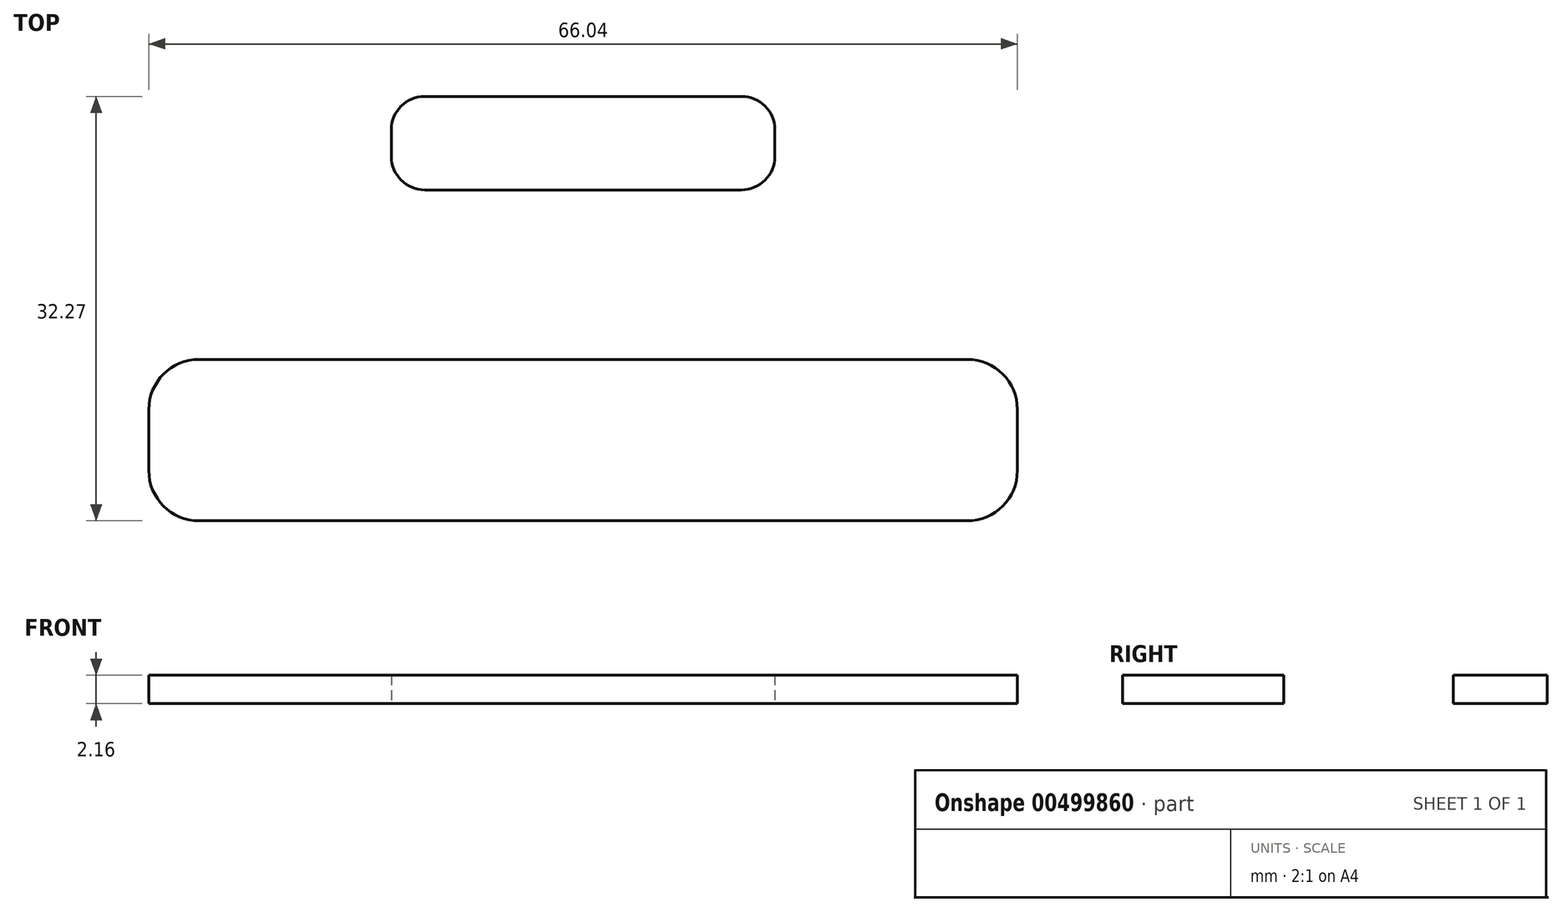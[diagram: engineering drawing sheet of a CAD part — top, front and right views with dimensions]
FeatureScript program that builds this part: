
annotation { "Feature Type Name" : "Feature", "Feature Type Description" : "" }
export const myFeature = defineFeature(function(context is Context, id is Id, definition is map)
    precondition{}
    {
        {
            var Q0;
            Q0=qCreatedBy(makeId("Top.planeOp"),FACE);
            var sketch = newSketch(context, id + "F0", { "sketchPlane" : qUnion([Q0])});
            skLineSegment(sketch, "E0.bottom", {"start": v(29.21, -6.13) * mm, "end": v(-29.21, -6.13) * mm});
            skLineSegment(sketch, "E0.top", {"start": v(29.21, 6.13) * mm, "end": v(-29.21, 6.13) * mm});
            skLineSegment(sketch, "E0.left", {"start": v(33.02, -2.32) * mm, "end": v(33.02, 2.32) * mm});
            skLineSegment(sketch, "E0.right", {"start": v(-33.02, -2.32) * mm, "end": v(-33.02, 2.32) * mm});
            skPoint(sketch, "E0.middle", {"position": v(0, 0) * mm});
            skLineSegment(sketch, "E1.bottom", {"start": v(12.04, 19.03) * mm, "end": v(-12.04, 19.03) * mm});
            skLineSegment(sketch, "E1.top", {"start": v(12.04, 26.14) * mm, "end": v(-12.04, 26.14) * mm});
            skLineSegment(sketch, "E1.left", {"start": v(14.58, 21.57) * mm, "end": v(14.58, 23.6) * mm});
            skLineSegment(sketch, "E1.right", {"start": v(-14.58, 21.57) * mm, "end": v(-14.58, 23.6) * mm});
            skPoint(sketch, "E1.middle", {"position": v(0, 22.59) * mm});
            skPoint(sketch, "E2.visualSharp", {"position": v(-14.58, 26.14) * mm});
            skArc(sketch, "E2.filletArc", {"start": v(-12.04, 26.14) * mm, "mid": v(-13.84, 25.4) * mm, "end": v(-14.58, 23.6) * mm});
            skPoint(sketch, "E3.visualSharp", {"position": v(-14.58, 19.03) * mm});
            skArc(sketch, "E3.filletArc", {"start": v(-14.58, 21.57) * mm, "mid": v(-13.84, 19.78) * mm, "end": v(-12.04, 19.03) * mm});
            skPoint(sketch, "E4.visualSharp", {"position": v(14.58, 19.03) * mm});
            skArc(sketch, "E4.filletArc", {"start": v(12.04, 19.03) * mm, "mid": v(13.84, 19.78) * mm, "end": v(14.58, 21.57) * mm});
            skPoint(sketch, "E5.visualSharp", {"position": v(14.58, 26.14) * mm});
            skArc(sketch, "E5.filletArc", {"start": v(14.58, 23.6) * mm, "mid": v(13.84, 25.4) * mm, "end": v(12.04, 26.14) * mm});
            skPoint(sketch, "E6.visualSharp", {"position": v(33.02, 6.13) * mm});
            skArc(sketch, "E6.filletArc", {"start": v(33.02, 2.32) * mm, "mid": v(31.9, 5.02) * mm, "end": v(29.21, 6.13) * mm});
            skPoint(sketch, "E7.visualSharp", {"position": v(33.02, -6.13) * mm});
            skArc(sketch, "E7.filletArc", {"start": v(29.21, -6.13) * mm, "mid": v(31.9, -5.02) * mm, "end": v(33.02, -2.32) * mm});
            skPoint(sketch, "E8.visualSharp", {"position": v(-33.02, -6.13) * mm});
            skArc(sketch, "E8.filletArc", {"start": v(-33.02, -2.32) * mm, "mid": v(-31.9, -5.02) * mm, "end": v(-29.21, -6.13) * mm});
            skPoint(sketch, "E9.visualSharp", {"position": v(-33.02, 6.13) * mm});
            skArc(sketch, "E9.filletArc", {"start": v(-29.21, 6.13) * mm, "mid": v(-31.9, 5.02) * mm, "end": v(-33.02, 2.32) * mm});
            skSolve(sketch);
        }
        {
            var Q0;
            Q0=makeQuery(id+"F0.imprint","IMPRINT",FACE,{"disambiguationData":[TD([[makeQuery(id+"F0.imprint","IMPRINT",EDGE,{"derivedFrom":sQuery(id+"F0.wireOp",EDGE,"E1.bottom")}),-1.0]])]});
            var Q1;
            Q1=makeQuery(id+"F0.imprint","IMPRINT",FACE,{"disambiguationData":[TD([[makeQuery(id+"F0.imprint","IMPRINT",EDGE,{"derivedFrom":sQuery(id+"F0.wireOp",EDGE,"E0.bottom")}),-1.0]])]});
            extrude(context, id + "F1", {"entities" : qUnion([Q0, Q1]), "depth" : 2.16 * mm});
        }
    });
